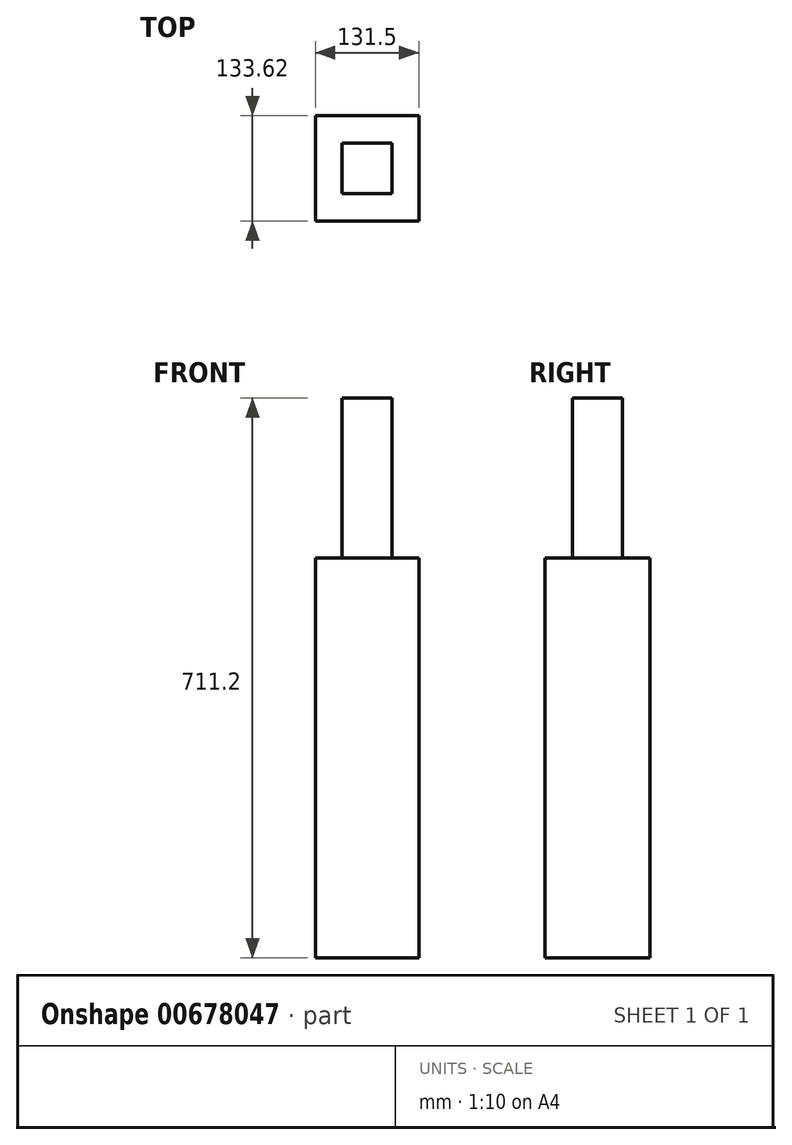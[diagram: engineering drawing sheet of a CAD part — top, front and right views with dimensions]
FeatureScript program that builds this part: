
annotation { "Feature Type Name" : "Feature", "Feature Type Description" : "" }
export const myFeature = defineFeature(function(context is Context, id is Id, definition is map)
    precondition{}
    {
        {
            var Q0;
            Q0=qCreatedBy(makeId("Top.planeOp"),FACE);
            var sketch = newSketch(context, id + "F0", { "sketchPlane" : qUnion([Q0])});
            skLineSegment(sketch, "E0.bottom", {"start": v(-65.75, 66.8) * mm, "end": v(65.75, 66.8) * mm});
            skLineSegment(sketch, "E0.top", {"start": v(-65.75, -66.8) * mm, "end": v(65.75, -66.8) * mm});
            skLineSegment(sketch, "E0.left", {"start": v(-65.75, 66.8) * mm, "end": v(-65.75, -66.8) * mm});
            skLineSegment(sketch, "E0.right", {"start": v(65.75, 66.8) * mm, "end": v(65.75, -66.8) * mm});
            skPoint(sketch, "E0.middle", {"position": v(0, 0) * mm});
            skSolve(sketch);
        }
        {
            var Q0;
            Q0=makeQuery(id+"F0.imprint","IMPRINT",FACE,{"disambiguationData":[TD([[makeQuery(id+"F0.imprint","IMPRINT",EDGE,{"derivedFrom":sQuery(id+"F0.wireOp",EDGE,"E0.bottom")}),-1.0]])]});
            extrude(context, id + "F1", {"entities" : qUnion([Q0]), "depth" : 508 * mm, "offsetDistance" : 25.4 * mm});
        }
        {
            var Q0;
            Q0=makeQuery(id+"F1.opExtrude","CAP_FACE",FACE,{"disambiguationData":[OSD([sQuery(id+"F0.wireOp",EDGE,"E0.bottom"),sQuery(id+"F0.wireOp",EDGE,"E0.top"),sQuery(id+"F0.wireOp",EDGE,"E0.left"),sQuery(id+"F0.wireOp",EDGE,"E0.right")])],"isStart":false});
            var sketch = newSketch(context, id + "F2", { "sketchPlane" : qUnion([Q0])});
            skLineSegment(sketch, "E1.bottom", {"start": v(-31.87, 31.87) * mm, "end": v(31.87, 31.87) * mm});
            skLineSegment(sketch, "E1.top", {"start": v(-31.87, -31.87) * mm, "end": v(31.87, -31.87) * mm});
            skLineSegment(sketch, "E1.left", {"start": v(-31.87, 31.87) * mm, "end": v(-31.87, -31.87) * mm});
            skLineSegment(sketch, "E1.right", {"start": v(31.87, 31.87) * mm, "end": v(31.87, -31.87) * mm});
            skPoint(sketch, "E1.middle", {"position": v(0, 0) * mm});
            skSolve(sketch);
        }
        {
            var Q0;
            Q0=makeQuery(id+"F2.imprint","IMPRINT",FACE,{"disambiguationData":[TD([[makeQuery(id+"F2.imprint","IMPRINT",EDGE,{"derivedFrom":sQuery(id+"F2.wireOp",EDGE,"E1.bottom")}),-1.0]])]});
            extrude(context, id + "F3", {"entities" : qUnion([Q0]), "operationType" : NewBodyOperationType.ADD, "depth" : 203.2 * mm, "offsetDistance" : 25.4 * mm});
        }
        {
            var Q0;
            Q0=makeQuery(id+"F3.opExtrude","CAP_FACE",FACE,{"disambiguationData":[OSD([sQuery(id+"F2.wireOp",EDGE,"E1.bottom"),sQuery(id+"F2.wireOp",EDGE,"E1.top"),sQuery(id+"F2.wireOp",EDGE,"E1.left"),sQuery(id+"F2.wireOp",EDGE,"E1.right")])],"isStart":false});
            var sketch = newSketch(context, id + "F4", { "sketchPlane" : qUnion([Q0])});
            skCircle(sketch, "E2", {"center": v(0, 3.07) * mm, "radius": 17.47 * mm});
            skCircle(sketch, "E3", {"center": v(0, 0) * mm, "radius": 21.55 * mm});
            skSolve(sketch);
        }
        {
            var Q0;
            Q0=sQuery(id+"F4.wireOp",EDGE,"E3");
            extrude(context, id + "F5", {"bodyType" : ToolBodyType.SURFACE, "surfaceEntities" : qUnion([Q0]), "depth" : 127 * mm, "offsetDistance" : 25.4 * mm});
        }
    });
